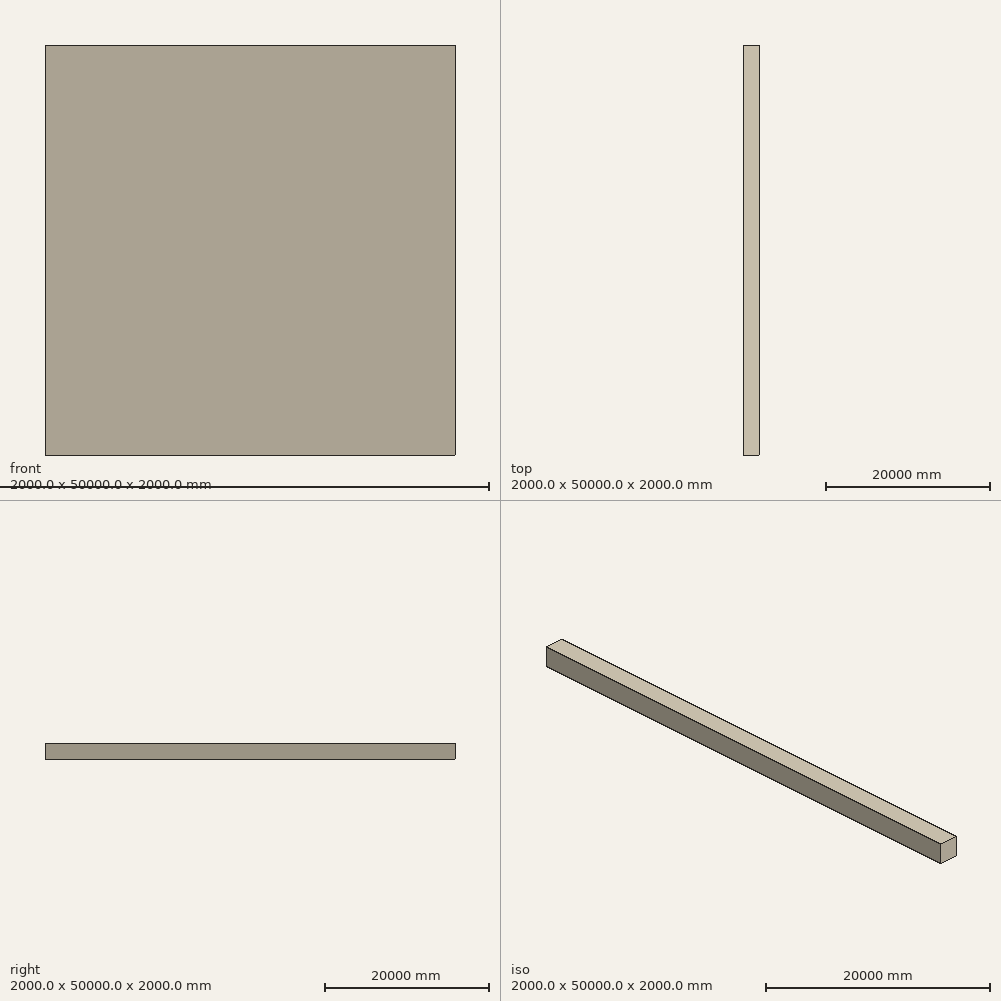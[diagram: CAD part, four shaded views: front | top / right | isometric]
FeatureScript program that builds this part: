
annotation { "Feature Type Name" : "Feature", "Feature Type Description" : "" }
export const myFeature = defineFeature(function(context is Context, id is Id, definition is map)
    precondition{}
    {
        {
            var Q0;
            Q0=qCreatedBy(makeId("Front.planeOp"),FACE);
            var sketch = newSketch(context, id + "F0", { "sketchPlane" : qUnion([Q0])});
            skLineSegment(sketch, "E0.bottom", {"start": v(0, 0) * mm, "end": v(2000, 0) * mm});
            skLineSegment(sketch, "E0.top", {"start": v(0, 2000) * mm, "end": v(2000, 2000) * mm});
            skLineSegment(sketch, "E0.left", {"start": v(0, 0) * mm, "end": v(0, 2000) * mm});
            skLineSegment(sketch, "E0.right", {"start": v(2000, 0) * mm, "end": v(2000, 2000) * mm});
            skSolve(sketch);
        }
        {
            var Q0;
            Q0 = qSketchRegion(id + "F0", true);
            extrude(context, id + "F1", {"entities" : qUnion([Q0]), "depth" : 50000 * mm});
        }
    });
